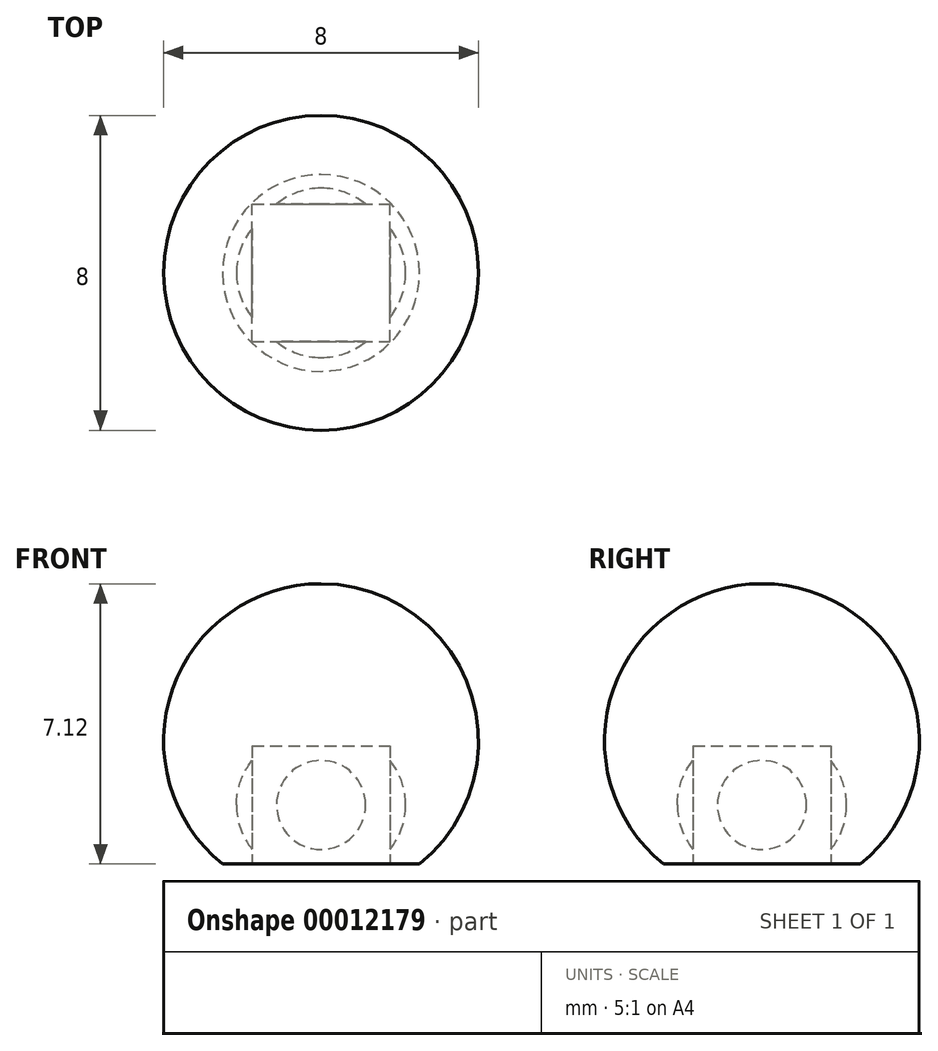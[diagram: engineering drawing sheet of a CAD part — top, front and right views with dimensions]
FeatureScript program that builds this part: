
annotation { "Feature Type Name" : "Feature", "Feature Type Description" : "" }
export const myFeature = defineFeature(function(context is Context, id is Id, definition is map)
    precondition{}
    {
        {
            var Q0;
            Q0=qCreatedBy(makeId("Front.planeOp"),FACE);
            var sketch = newSketch(context, id + "F0", { "sketchPlane" : qUnion([Q0])});
            skLineSegment(sketch, "E0", {"start": v(0, 0) * mm, "end": v(0, 7.12) * mm});
            skPoint(sketch, "E1.orphan", {"position": v(-4.65, 0) * mm});
            skLineSegment(sketch, "E2", {"start": v(0, 0) * mm, "end": v(2.5, 0) * mm});
            skArc(sketch, "E3", {"start": v(2.5, 0) * mm, "mid": v(3.77, 4.45) * mm, "end": v(0, 7.12) * mm});
            skLineSegment(sketch, "E4", {"start": v(0, 3) * mm, "end": v(1.75, 3) * mm, "construction": true});
            skLineSegment(sketch, "E5", {"start": v(1.75, 3) * mm, "end": v(1.75, 0) * mm, "construction": true});
            skSolve(sketch);
        }
        {
            var Q0;
            Q0=makeQuery(id+"F0.imprint","IMPRINT",FACE,{"disambiguationData":[TD([[makeQuery(id+"F0.imprint","IMPRINT",EDGE,{"derivedFrom":sQuery(id+"F0.wireOp",EDGE,"E0")}),-1.0]])]});
            var Q1;
            Q1=sQuery(id+"F0.wireOp",EDGE,"E0");
            revolve(context, id + "F1", {"entities" : qUnion([Q0]), "axis" : qUnion([Q1]), "revolveType" : RevolveType.FULL});
        }
        {
            var Q0;
            Q0=makeQuery(id+"F1.opRevolve","SWEPT_FACE",FACE,{"disambiguationData":[OSD([sQuery(id+"F0.wireOp",EDGE,"E2")])]});
            var sketch = newSketch(context, id + "F2", { "sketchPlane" : qUnion([Q0])});
            skLineSegment(sketch, "E6.bottom", {"start": v(-1.75, 1.75) * mm, "end": v(1.75, 1.75) * mm});
            skLineSegment(sketch, "E6.top", {"start": v(-1.75, -1.75) * mm, "end": v(1.75, -1.75) * mm});
            skLineSegment(sketch, "E6.left", {"start": v(-1.75, 1.75) * mm, "end": v(-1.75, -1.75) * mm});
            skLineSegment(sketch, "E6.right", {"start": v(1.75, 1.75) * mm, "end": v(1.75, -1.75) * mm});
            skLineSegment(sketch, "E7", {"start": v(-1.75, 1.75) * mm, "end": v(1.75, -1.75) * mm});
            skSolve(sketch);
        }
        {
            var Q0;
            Q0=makeQuery(id+"F2.imprint","IMPRINT",FACE,{"disambiguationData":[TD([[makeQuery(id+"F2.imprint","IMPRINT",EDGE,{"derivedFrom":sQuery(id+"F2.wireOp",EDGE,"E6.bottom")}),-1.0]])]});
            var Q1;
            Q1=makeQuery(id+"F2.imprint","IMPRINT",FACE,{"disambiguationData":[TD([[makeQuery(id+"F2.imprint","IMPRINT",EDGE,{"derivedFrom":sQuery(id+"F2.wireOp",EDGE,"E6.top")}),1.0]])]});
            extrude(context, id + "F3", {"entities" : qUnion([Q0, Q1]), "operationType" : NewBodyOperationType.REMOVE, "oppositeDirection" : true, "depth" : 3 * mm});
        }
        {
            var Q0;
            Q0=makeQuery(id+"F3.boolean.opBoolean","COPY",FACE,{"derivedFrom":makeQuery(id+"F3.opExtrude","SWEPT_FACE",FACE,{"disambiguationData":[OSD([sQuery(id+"F2.wireOp",EDGE,"E6.top")])]})});
            var Q1;
            Q1=makeQuery(id+"F3.boolean.opBoolean","COPY",FACE,{"derivedFrom":makeQuery(id+"F3.opExtrude","SWEPT_FACE",FACE,{"disambiguationData":[OSD([sQuery(id+"F2.wireOp",EDGE,"E6.bottom")])]})});
            cPlane(context, id + "F4", {"entities" : qUnion([Q0, Q1]), "cplaneType" : CPlaneType.MID_PLANE, "offset" : 150 * mm, "width" : 150 * mm, "height" : 150 * mm});
        }
        {
            var Q0;
            Q0=qCreatedBy(id+"F4.planeOp",FACE);
            var sketch = newSketch(context, id + "F5", { "sketchPlane" : qUnion([Q0])});
            skArc(sketch, "E8", {"start": v(2.15, 1.5) * mm, "mid": v(2.05, 2.1) * mm, "end": v(1.75, 2.63) * mm});
            skLineSegment(sketch, "E9.0", {"start": v(1.75, 3) * mm, "end": v(1.75, 0) * mm, "construction": true});
            skLineSegment(sketch, "E10", {"start": v(1.75, 1.5) * mm, "end": v(1.75, 2.63) * mm});
            skLineSegment(sketch, "E11", {"start": v(2.15, 1.5) * mm, "end": v(1.75, 1.5) * mm});
            skSolve(sketch);
        }
        {
            var Q0;
            Q0 = qSketchRegion(id + "F5", true);
            var Q1;
            Q1=sQuery(id+"F5.wireOp",EDGE,"E11");
            revolve(context, id + "F6", {"operationType" : NewBodyOperationType.REMOVE, "entities" : qUnion([Q0]), "axis" : qUnion([Q1]), "revolveType" : RevolveType.FULL, "oppositeDirection" : true});
        }
        {
            var Q0;
            Q0=qCreatedBy(id+"F4.planeOp",FACE);
            var sketch = newSketch(context, id + "F7", { "sketchPlane" : qUnion([Q0])});
            skLineSegment(sketch, "E12", {"start": v(0, 0) * mm, "end": v(0, 4.75) * mm});
            skSolve(sketch);
        }
        {
            var Q0;
            Q0=makeQuery(id+"F6.boolean.opBoolean","COPY",FACE,{"derivedFrom":makeQuery(id+"F6.opRevolve","SWEPT_FACE",FACE,{"disambiguationData":[OSD([sQuery(id+"F5.wireOp",EDGE,"E8")])]})});
            var Q1;
            Q1=sQuery(id+"F7.wireOp",EDGE,"E12");
            circularPattern(context, id + "F8", {"faces" : qUnion([Q0]), "axis" : qUnion([Q1]), "angle" : 90 * degree, "instanceCount" : 4, "patternType" : PatternType.FACE});
        }
    });
